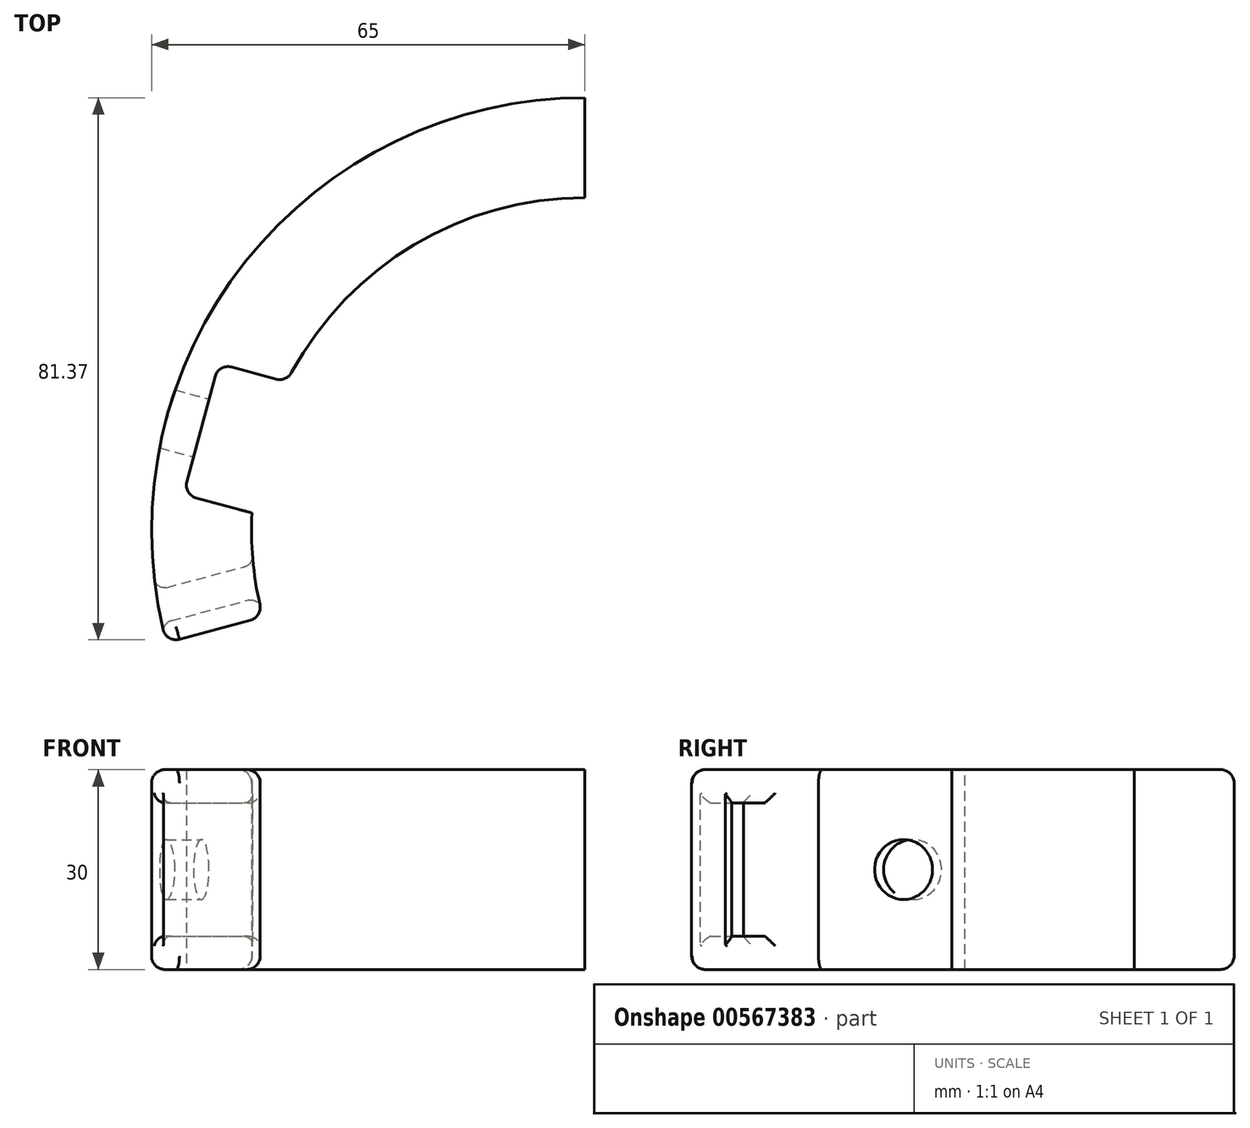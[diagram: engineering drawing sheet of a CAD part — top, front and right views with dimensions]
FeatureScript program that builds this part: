
annotation { "Feature Type Name" : "Feature", "Feature Type Description" : "" }
export const myFeature = defineFeature(function(context is Context, id is Id, definition is map)
    precondition{}
    {
        {
            var Q0;
            Q0=qCreatedBy(makeId("Top.planeOp"),FACE);
            var sketch = newSketch(context, id + "F0", { "sketchPlane" : qUnion([Q0])});
            skArc(sketch, "E0", {"start": v(0, 50) * mm, "mid": v(-39.67, 30.44) * mm, "end": v(-48.3, -12.94) * mm});
            skArc(sketch, "E1", {"start": v(0, 65) * mm, "mid": v(-51.57, 39.57) * mm, "end": v(-62.79, -16.82) * mm});
            skLineSegment(sketch, "E2", {"start": v(0, 0) * mm, "end": v(0, 95.99) * mm, "construction": true});
            skLineSegment(sketch, "E3", {"start": v(0, 0) * mm, "end": v(-96.7, -25.91) * mm, "construction": true});
            skLineSegment(sketch, "E4", {"start": v(0, 65) * mm, "end": v(0, 50) * mm});
            skLineSegment(sketch, "E5", {"start": v(-48.3, -12.94) * mm, "end": v(-62.79, -16.82) * mm});
            skSolve(sketch);
        }
        {
            var Q0;
            Q0 = qSketchRegion(id + "F0", true);
            extrude(context, id + "F1", {"entities" : qUnion([Q0]), "depth" : 30 * mm, "offsetDistance" : 25 * mm});
        }
        {
            var Q0;
            Q0=qCreatedBy(makeId("Top.planeOp"),FACE);
            var sketch = newSketch(context, id + "F2", { "sketchPlane" : qUnion([Q0])});
            skLineSegment(sketch, "E6", {"start": v(0, 0) * mm, "end": v(0, 70.67) * mm, "construction": true});
            skLineSegment(sketch, "E7", {"start": v(0, 0) * mm, "end": v(-74.97, 20.09) * mm, "construction": true});
            skPoint(sketch, "E8", {"position": v(-48.35, 12.96) * mm});
            skLineSegment(sketch, "E9", {"start": v(-48.35, 12.96) * mm, "end": v(-58.44, 15.66) * mm, "construction": true});
            skLineSegment(sketch, "E10", {"start": v(-49.93, 2.66) * mm, "end": v(-60.23, 5.42) * mm});
            skLineSegment(sketch, "E11", {"start": v(-44.73, 22.34) * mm, "end": v(-54.96, 25.08) * mm});
            skLineSegment(sketch, "E12", {"start": v(-54.96, 25.08) * mm, "end": v(-60.23, 5.42) * mm});
            skPoint(sketch, "E13", {"position": v(-57.55, 15.42) * mm});
            skArc(sketch, "E14", {"start": v(-44.73, 22.34) * mm, "mid": v(-48.34, 12.77) * mm, "end": v(-49.93, 2.66) * mm});
            skSolve(sketch);
        }
        {
            var Q0;
            Q0 = qSketchRegion(id + "F2", true);
            extrude(context, id + "F3", {"entities" : qUnion([Q0]), "operationType" : NewBodyOperationType.REMOVE, "depth" : 30 * mm, "offsetDistance" : 25 * mm});
        }
        {
            var Q0;
            Q0=makeQuery(id+"F3.boolean.opBoolean","COPY",FACE,{"derivedFrom":makeQuery(id+"F3.opExtrude","SWEPT_FACE",FACE,{"disambiguationData":[OSD([sQuery(id+"F2.wireOp",EDGE,"E12")])]})});
            cPlane(context, id + "F4", {"entities" : qUnion([Q0]), "cplaneType" : CPlaneType.OFFSET, "offset" : 0 * mm, "width" : 150 * mm, "height" : 150 * mm});
        }
        {
            var Q0;
            Q0=qCreatedBy(id+"F4.planeOp",FACE);
            var sketch = newSketch(context, id + "F5", { "sketchPlane" : qUnion([Q0])});
            skLineSegment(sketch, "E15", {"start": v(0, 15) * mm, "end": v(9.94, 15) * mm, "construction": true});
            skLineSegment(sketch, "E16", {"start": v(9.94, 15) * mm, "end": v(-12.25, 15) * mm, "construction": true});
            skPoint(sketch, "E17.start.orphan", {"position": v(0, 32.96) * mm});
            skLineSegment(sketch, "E18", {"start": v(0, 15) * mm, "end": v(0, 31.2) * mm, "construction": true});
            skLineSegment(sketch, "E19", {"start": v(0, 31.2) * mm, "end": v(0, -4.52) * mm, "construction": true});
            skLineSegment(sketch, "E20", {"start": v(0, 19.5) * mm, "end": v(0, 19.5) * mm});
            skCircle(sketch, "E21", {"center": v(0, 15) * mm, "radius": 4.5 * mm});
            skSolve(sketch);
        }
        {
            var Q0;
            Q0=makeQuery(id+"F5.imprint","IMPRINT",FACE,{"disambiguationData":[TD([[makeQuery(id+"F5.imprint","IMPRINT",EDGE,{"derivedFrom":sQuery(id+"F5.wireOp",EDGE,"E21")}),1.0]])]});
            extrude(context, id + "F6", {"entities" : qUnion([Q0]), "operationType" : NewBodyOperationType.REMOVE, "oppositeDirection" : true, "depth" : 25 * mm, "offsetDistance" : 25 * mm});
        }
        {
            var Q0;
            Q0=makeQuery(id+"F1.opExtrude","SWEPT_FACE",FACE,{"disambiguationData":[OSD([sQuery(id+"F0.wireOp",EDGE,"E5")])]});
            cPlane(context, id + "F7", {"entities" : qUnion([Q0]), "cplaneType" : CPlaneType.OFFSET, "offset" : 3 * mm, "oppositeDirection" : true, "width" : 150 * mm, "height" : 150 * mm});
        }
        {
            var Q0;
            Q0=qCreatedBy(id+"F7.planeOp",FACE);
            var sketch = newSketch(context, id + "F8", { "sketchPlane" : qUnion([Q0])});
            skLineSegment(sketch, "E22", {"start": v(0, 0) * mm, "end": v(-107.44, 0) * mm, "construction": true});
            skLineSegment(sketch, "E23", {"start": v(0, 0) * mm, "end": v(0, 30) * mm, "construction": true});
            skLineSegment(sketch, "E24", {"start": v(0, 30) * mm, "end": v(-86.2, 30) * mm, "construction": true});
            skPoint(sketch, "E25", {"position": v(-69.29, 0) * mm});
            skPoint(sketch, "E26", {"position": v(-69.29, 30) * mm});
            skLineSegment(sketch, "E27", {"start": v(-69.29, 30) * mm, "end": v(-60, 30) * mm, "construction": true});
            skLineSegment(sketch, "E28", {"start": v(-60, 30) * mm, "end": v(-60, 0) * mm, "construction": true});
            skLineSegment(sketch, "E29", {"start": v(-60, 0) * mm, "end": v(-60, 5) * mm, "construction": true});
            skLineSegment(sketch, "E30", {"start": v(-60, 30) * mm, "end": v(-60, 25) * mm, "construction": true});
            skLineSegment(sketch, "E31", {"start": v(-69.29, 30) * mm, "end": v(-69.29, 0) * mm, "construction": true});
            skLineSegment(sketch, "E32", {"start": v(-60, 25) * mm, "end": v(-69.29, 25) * mm});
            skLineSegment(sketch, "E33", {"start": v(-69.29, 25) * mm, "end": v(-69.29, 5) * mm});
            skLineSegment(sketch, "E34", {"start": v(-69.29, 5) * mm, "end": v(-60, 5) * mm});
            skPoint(sketch, "E35", {"position": v(-47.74, 30) * mm});
            skPoint(sketch, "E36", {"position": v(-47.74, 0) * mm});
            skLineSegment(sketch, "E37", {"start": v(-47.74, 30) * mm, "end": v(-47.74, 0) * mm, "construction": true});
            skLineSegment(sketch, "E38", {"start": v(-69.29, 25) * mm, "end": v(-47.74, 25) * mm});
            skLineSegment(sketch, "E39", {"start": v(-69.29, 5) * mm, "end": v(-47.74, 5) * mm});
            skLineSegment(sketch, "E40", {"start": v(-47.74, 5) * mm, "end": v(-47.74, 25) * mm});
            skSolve(sketch);
        }
        {
            var Q0;
            Q0 = qSketchRegion(id + "F8", true);
            extrude(context, id + "F9", {"entities" : qUnion([Q0]), "operationType" : NewBodyOperationType.REMOVE, "oppositeDirection" : true, "depth" : 5 * mm, "offsetDistance" : 25 * mm});
        }
        {
            var Q0;
            Q0=makeQuery(id+"F3.boolean.opBoolean","COPY",EDGE,{"derivedFrom":makeQuery(id+"F3.opExtrude","SWEPT_EDGE",EDGE,{"disambiguationData":[OSD([sQuery(id+"F2.wireOp",EDGE,"E11"),sQuery(id+"F2.wireOp",EDGE,"wfyfxPfv-1SoC-H9iN-YqKZ-98JUiyJ8nlxa")])]})});
            fillet(context, id + "F10", {"entities" : qUnion([Q0]), "radius" : 2 * mm, "tangentPropagation" : true, "allowEdgeOverflow" : false});
        }
        {
            var Q0;
            Q0=makeQuery(id+"F3.boolean.opBoolean","COPY",EDGE,{"derivedFrom":makeQuery(id+"F3.opExtrude","SWEPT_EDGE",EDGE,{"disambiguationData":[OSD([sQuery(id+"F2.wireOp",EDGE,"E10"),sQuery(id+"F2.wireOp",EDGE,"wfyfxPfv-1SoC-H9iN-YqKZ-98JUiyJ8nlxa")])]})});
            fillet(context, id + "F11", {"entities" : qUnion([Q0]), "radius" : 2 * mm, "tangentPropagation" : true, "allowEdgeOverflow" : false});
        }
        {
            var Q0;
            Q0=makeQuery(id+"F1.opExtrude","SWEPT_EDGE",EDGE,{"disambiguationData":[OSD([sQuery(id+"F0.wireOp",EDGE,"E0"),sQuery(id+"F0.wireOp",EDGE,"E5")])]});
            fillet(context, id + "F12", {"entities" : qUnion([Q0]), "radius" : 2 * mm, "tangentPropagation" : true, "allowEdgeOverflow" : false});
        }
        {
            var Q0;
            {var subQ0=sQuery(id+"F0.wireOp",EDGE,"E5");var subQ1=sQuery(id+"F0.wireOp",EDGE,"E0");Q0=makeQuery(id+"F12.opFillet","BLEND_EDGE",EDGE,{"blendedFrom":[makeQuery(id+"F1.opExtrude","SWEPT_EDGE",EDGE,{"disambiguationData":[OSD([subQ1,subQ0])]}),makeQuery(id+"F1.opExtrude","CAP_FACE",FACE,{"disambiguationData":[OSD([subQ1,sQuery(id+"F0.wireOp",EDGE,"E1"),sQuery(id+"F0.wireOp",EDGE,"E4"),subQ0])],"isStart":true})],"blendedInto":[makeQuery(id+"F1.opExtrude","CAP_FACE",FACE,{"disambiguationData":[OSD([subQ1,sQuery(id+"F0.wireOp",EDGE,"E1"),sQuery(id+"F0.wireOp",EDGE,"E4"),subQ0])],"isStart":true})]});}
            fillet(context, id + "F13", {"entities" : qUnion([Q0]), "radius" : 2 * mm, "tangentPropagation" : true, "allowEdgeOverflow" : false});
        }
        {
            var Q0;
            {var subQ0=sQuery(id+"F0.wireOp",EDGE,"E0");var subQ1=sQuery(id+"F0.wireOp",EDGE,"E5");Q0=makeQuery(id+"F3.boolean.opBoolean","SPLIT",EDGE,{"disambiguationData":[TD([makeQuery(id+"F1.opExtrude","SWEPT_FACE",FACE,{"disambiguationData":[OSD([subQ1])]})])],"derivedFrom":makeQuery(id+"F1.opExtrude","CAP_EDGE",EDGE,{"disambiguationData":[OSD([subQ0])],"isStart":false})});}
            fillet(context, id + "F14", {"entities" : qUnion([Q0]), "radius" : 2 * mm, "tangentPropagation" : true, "allowEdgeOverflow" : false});
        }
        {
            var Q0;
            {var subQ0=sQuery(id+"F0.wireOp",EDGE,"E5");var subQ3=sQuery(id+"F0.wireOp",EDGE,"E0");Q0=makeQuery(id+"F9.boolean.opBoolean","INTERSECT",EDGE,{"derivedFrom":[makeQuery(id+"F3.boolean.opBoolean","SPLIT",FACE,{"disambiguationData":[TD([makeQuery(id+"F1.opExtrude","SWEPT_FACE",FACE,{"disambiguationData":[OSD([subQ0])]})])],"derivedFrom":makeQuery(id+"F1.opExtrude","SWEPT_FACE",FACE,{"disambiguationData":[OSD([subQ3])]})}),makeQuery(id+"F9.opExtrude","CAP_FACE",FACE,{"disambiguationData":[OSD([sQuery(id+"F8.wireOp",EDGE,"E38"),sQuery(id+"F8.wireOp",EDGE,"E39"),sQuery(id+"F8.wireOp",EDGE,"E40"),sQuery(id+"F8.wireOp",EDGE,"E33")])],"isStart":false})]});}
            var Q1;
            {var subQ0=sQuery(id+"F0.wireOp",EDGE,"E5");var subQ3=sQuery(id+"F0.wireOp",EDGE,"E0");Q1=makeQuery(id+"F9.boolean.opBoolean","INTERSECT",EDGE,{"derivedFrom":[makeQuery(id+"F3.boolean.opBoolean","SPLIT",FACE,{"disambiguationData":[TD([makeQuery(id+"F1.opExtrude","SWEPT_FACE",FACE,{"disambiguationData":[OSD([subQ0])]})])],"derivedFrom":makeQuery(id+"F1.opExtrude","SWEPT_FACE",FACE,{"disambiguationData":[OSD([subQ3])]})}),makeQuery(id+"F9.opExtrude","SWEPT_FACE",FACE,{"disambiguationData":[OSD([sQuery(id+"F8.wireOp",EDGE,"E38")])]})]});}
            var Q2;
            {var subQ0=sQuery(id+"F0.wireOp",EDGE,"E5");var subQ3=sQuery(id+"F0.wireOp",EDGE,"E0");Q2=makeQuery(id+"F9.boolean.opBoolean","INTERSECT",EDGE,{"derivedFrom":[makeQuery(id+"F3.boolean.opBoolean","SPLIT",FACE,{"disambiguationData":[TD([makeQuery(id+"F1.opExtrude","SWEPT_FACE",FACE,{"disambiguationData":[OSD([subQ0])]})])],"derivedFrom":makeQuery(id+"F1.opExtrude","SWEPT_FACE",FACE,{"disambiguationData":[OSD([subQ3])]})}),makeQuery(id+"F9.opExtrude","CAP_FACE",FACE,{"disambiguationData":[OSD([sQuery(id+"F8.wireOp",EDGE,"E38"),sQuery(id+"F8.wireOp",EDGE,"E39"),sQuery(id+"F8.wireOp",EDGE,"E40"),sQuery(id+"F8.wireOp",EDGE,"E33")])],"isStart":true})]});}
            var Q3;
            {var subQ0=sQuery(id+"F0.wireOp",EDGE,"E5");var subQ3=sQuery(id+"F0.wireOp",EDGE,"E0");Q3=makeQuery(id+"F9.boolean.opBoolean","INTERSECT",EDGE,{"derivedFrom":[makeQuery(id+"F3.boolean.opBoolean","SPLIT",FACE,{"disambiguationData":[TD([makeQuery(id+"F1.opExtrude","SWEPT_FACE",FACE,{"disambiguationData":[OSD([subQ0])]})])],"derivedFrom":makeQuery(id+"F1.opExtrude","SWEPT_FACE",FACE,{"disambiguationData":[OSD([subQ3])]})}),makeQuery(id+"F9.opExtrude","SWEPT_FACE",FACE,{"disambiguationData":[OSD([sQuery(id+"F8.wireOp",EDGE,"E39")])]})]});}
            fillet(context, id + "F15", {"entities" : qUnion([Q0, Q1, Q2, Q3]), "radius" : 1.5 * mm, "tangentPropagation" : true, "allowEdgeOverflow" : false});
        }
        {
            var Q0;
            Q0=makeQuery(id+"F1.opExtrude","CAP_EDGE",EDGE,{"disambiguationData":[OSD([sQuery(id+"F0.wireOp",EDGE,"E1")])],"isStart":true});
            fillet(context, id + "F16", {"entities" : qUnion([Q0]), "radius" : 2 * mm, "tangentPropagation" : true, "allowEdgeOverflow" : false});
        }
        {
            var Q0;
            Q0=makeQuery(id+"F9.boolean.opBoolean","INTERSECT",EDGE,{"derivedFrom":[makeQuery(id+"F1.opExtrude","SWEPT_FACE",FACE,{"disambiguationData":[OSD([sQuery(id+"F0.wireOp",EDGE,"E1")])]}),makeQuery(id+"F9.opExtrude","SWEPT_FACE",FACE,{"disambiguationData":[OSD([sQuery(id+"F8.wireOp",EDGE,"E38")])]})]});
            var Q1;
            Q1=makeQuery(id+"F9.boolean.opBoolean","INTERSECT",EDGE,{"derivedFrom":[makeQuery(id+"F1.opExtrude","SWEPT_FACE",FACE,{"disambiguationData":[OSD([sQuery(id+"F0.wireOp",EDGE,"E1")])]}),makeQuery(id+"F9.opExtrude","CAP_FACE",FACE,{"disambiguationData":[OSD([sQuery(id+"F8.wireOp",EDGE,"E38"),sQuery(id+"F8.wireOp",EDGE,"E39"),sQuery(id+"F8.wireOp",EDGE,"E40"),sQuery(id+"F8.wireOp",EDGE,"E33")])],"isStart":true})]});
            var Q2;
            Q2=makeQuery(id+"F9.boolean.opBoolean","INTERSECT",EDGE,{"derivedFrom":[makeQuery(id+"F1.opExtrude","SWEPT_FACE",FACE,{"disambiguationData":[OSD([sQuery(id+"F0.wireOp",EDGE,"E1")])]}),makeQuery(id+"F9.opExtrude","SWEPT_FACE",FACE,{"disambiguationData":[OSD([sQuery(id+"F8.wireOp",EDGE,"E39")])]})]});
            var Q3;
            Q3=makeQuery(id+"F9.boolean.opBoolean","INTERSECT",EDGE,{"derivedFrom":[makeQuery(id+"F1.opExtrude","SWEPT_FACE",FACE,{"disambiguationData":[OSD([sQuery(id+"F0.wireOp",EDGE,"E1")])]}),makeQuery(id+"F9.opExtrude","CAP_FACE",FACE,{"disambiguationData":[OSD([sQuery(id+"F8.wireOp",EDGE,"E38"),sQuery(id+"F8.wireOp",EDGE,"E39"),sQuery(id+"F8.wireOp",EDGE,"E40"),sQuery(id+"F8.wireOp",EDGE,"E33")])],"isStart":false})]});
            fillet(context, id + "F17", {"entities" : qUnion([Q0, Q1, Q2, Q3]), "radius" : 1.5 * mm, "tangentPropagation" : true, "allowEdgeOverflow" : false});
        }
    });
